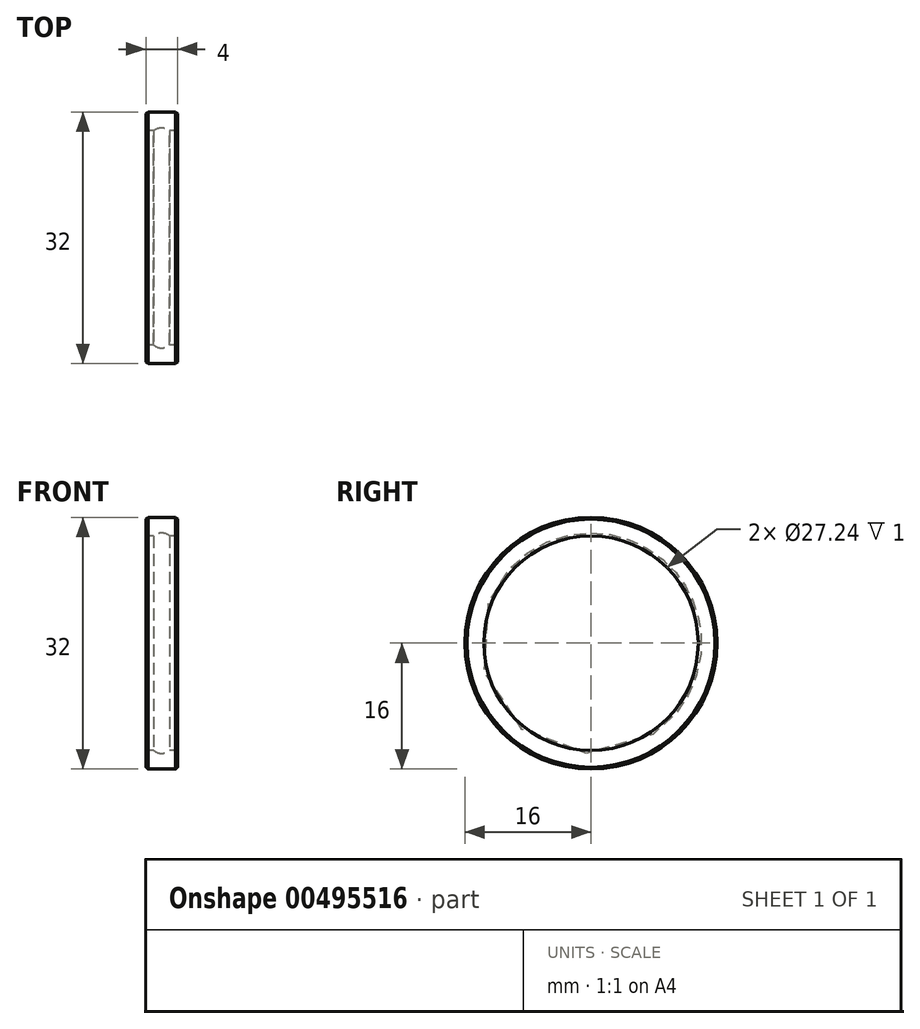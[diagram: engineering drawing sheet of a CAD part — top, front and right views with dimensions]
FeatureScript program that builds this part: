
annotation { "Feature Type Name" : "Feature", "Feature Type Description" : "" }
export const myFeature = defineFeature(function(context is Context, id is Id, definition is map)
    precondition{}
    {
        {
            var Q0;
            Q0=qCreatedBy(makeId("Front.planeOp"),FACE);
            var sketch = newSketch(context, id + "F0", { "sketchPlane" : qUnion([Q0])});
            skArc(sketch, "E0", {"start": v(1, 13.62) * mm, "mid": v(0.54, 13.9) * mm, "end": v(0, 14) * mm});
            skLineSegment(sketch, "E1.bottom", {"start": v(0, 14) * mm, "end": v(0, 14) * mm});
            skLineSegment(sketch, "E1.top", {"start": v(0, 16) * mm, "end": v(0, 16) * mm});
            skLineSegment(sketch, "E1.left", {"start": v(0, 14) * mm, "end": v(0, 16) * mm});
            skLineSegment(sketch, "E1.right", {"start": v(0, 14) * mm, "end": v(0, 16) * mm, "construction": true});
            skLineSegment(sketch, "E2", {"start": v(0, 16) * mm, "end": v(2, 16) * mm});
            skLineSegment(sketch, "E3", {"start": v(2, 16) * mm, "end": v(2, 13.62) * mm});
            skLineSegment(sketch, "E4", {"start": v(2, 13.62) * mm, "end": v(1, 13.62) * mm});
            skPoint(sketch, "E5", {"position": v(1, 16) * mm});
            skLineSegment(sketch, "E6.MirrorCS", {"start": v(-2, 13.62) * mm, "end": v(-1, 13.62) * mm});
            skArc(sketch, "E7.MirrorCS", {"start": v(-1, 13.62) * mm, "mid": v(-0.54, 13.9) * mm, "end": v(0, 14) * mm});
            skLineSegment(sketch, "E8.MirrorCS", {"start": v(0, 16) * mm, "end": v(-2, 16) * mm});
            skPoint(sketch, "E9.MirrorP", {"position": v(-1, 16) * mm});
            skLineSegment(sketch, "E10.MirrorCS", {"start": v(-2, 16) * mm, "end": v(-2, 13.62) * mm});
            skLineSegment(sketch, "E11", {"start": v(24.66, 0) * mm, "end": v(32.2, 0) * mm, "construction": true});
            skSolve(sketch);
        }
        {
            var Q0;
            Q0=makeQuery(id+"F0.imprint","IMPRINT",FACE,{"disambiguationData":[TD([[makeQuery(id+"F0.imprint","IMPRINT",EDGE,{"derivedFrom":sQuery(id+"F0.wireOp",EDGE,"E6.MirrorCS")}),1.0]])]});
            var Q1;
            Q1=makeQuery(id+"F0.imprint","IMPRINT",FACE,{"disambiguationData":[TD([[makeQuery(id+"F0.imprint","IMPRINT",EDGE,{"derivedFrom":sQuery(id+"F0.wireOp",EDGE,"E0")}),-1.0]])]});
            var Q2;
            Q2=sQuery(id+"F0.wireOp",EDGE,"E11");
            revolve(context, id + "F1", {"entities" : qUnion([Q0, Q1]), "axis" : qUnion([Q2]), "revolveType" : RevolveType.FULL});
        }
        {
            var Q0;
            Q0=makeQuery(id+"F1.opRevolve","SWEPT_EDGE",EDGE,{"disambiguationData":[OSD([sQuery(id+"F0.wireOp",EDGE,"E8.MirrorCS"),sQuery(id+"F0.wireOp",EDGE,"E10.MirrorCS")])]});
            var Q1;
            Q1=makeQuery(id+"F1.opRevolve","SWEPT_EDGE",EDGE,{"disambiguationData":[OSD([sQuery(id+"F0.wireOp",EDGE,"E2"),sQuery(id+"F0.wireOp",EDGE,"E3")])]});
            chamfer(context, id + "F2", {"entities" : qUnion([Q0, Q1]), "width" : .25 * mm, "tangentPropagation" : true});
        }
    });
